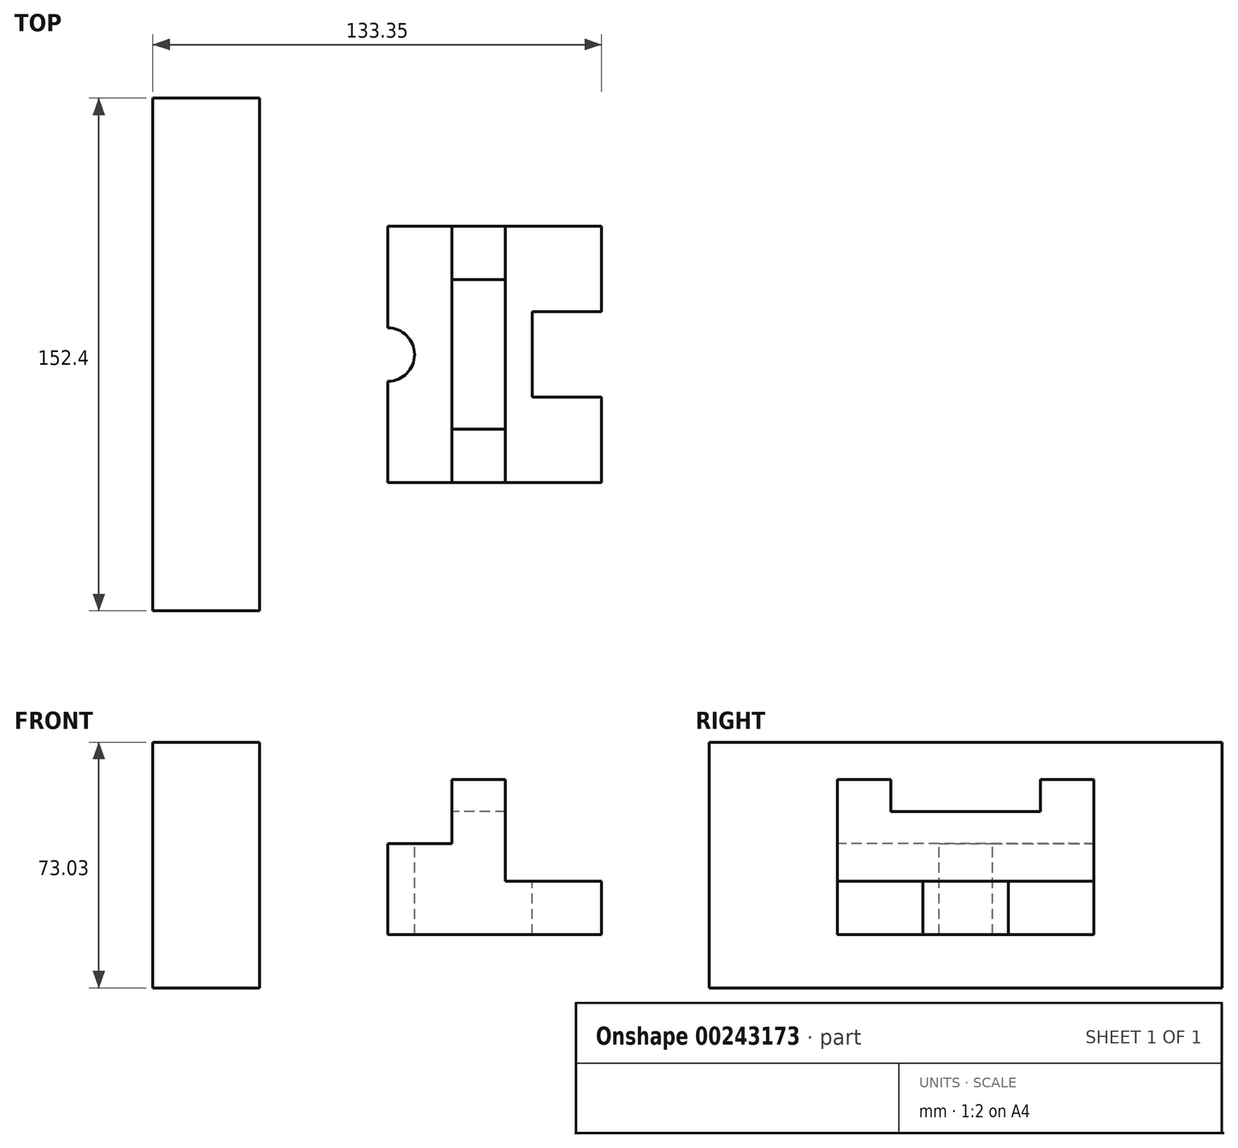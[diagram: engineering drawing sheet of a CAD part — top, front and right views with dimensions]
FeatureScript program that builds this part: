
annotation { "Feature Type Name" : "Feature", "Feature Type Description" : "" }
export const myFeature = defineFeature(function(context is Context, id is Id, definition is map)
    precondition{}
    {
        {
            var Q0;
            Q0=qCreatedBy(makeId("Top.planeOp"),FACE);
            var sketch = newSketch(context, id + "F0", { "sketchPlane" : qUnion([Q0])});
            skLineSegment(sketch, "E0", {"start": v(0, 0) * mm, "end": v(0, 76.2) * mm});
            skLineSegment(sketch, "E1", {"start": v(0, 0) * mm, "end": v(0, -76.2) * mm});
            skLineSegment(sketch, "E2", {"start": v(-127, 0) * mm, "end": v(-127, 76.2) * mm});
            skLineSegment(sketch, "E3", {"start": v(-127, 0) * mm, "end": v(-127, -76.2) * mm});
            skLineSegment(sketch, "E4", {"start": v(-127, 76.2) * mm, "end": v(0, 76.2) * mm});
            skLineSegment(sketch, "E5", {"start": v(-127, -76.2) * mm, "end": v(0, -76.2) * mm});
            skLineSegment(sketch, "E6", {"start": v(-127, 76.2) * mm, "end": v(-127, 25.4) * mm});
            skLineSegment(sketch, "E7", {"start": v(-127, -76.2) * mm, "end": v(-127, -25.4) * mm});
            skLineSegment(sketch, "E8", {"start": v(-127, -76.2) * mm, "end": v(-69.85, -76.2) * mm});
            skLineSegment(sketch, "E9", {"start": v(-127, 76.2) * mm, "end": v(-69.85, 76.2) * mm});
            skLineSegment(sketch, "E10", {"start": v(-127, 25.4) * mm, "end": v(-85.72, 25.4) * mm});
            skLineSegment(sketch, "E11", {"start": v(-127, -25.4) * mm, "end": v(-85.72, -25.4) * mm});
            skLineSegment(sketch, "E12", {"start": v(-85.72, 25.4) * mm, "end": v(-85.72, -25.4) * mm});
            skLineSegment(sketch, "E13", {"start": v(-69.85, 76.2) * mm, "end": v(-69.85, -76.2) * mm});
            skLineSegment(sketch, "E14", {"start": v(-69.85, 76.2) * mm, "end": v(-38.1, 76.2) * mm});
            skLineSegment(sketch, "E15", {"start": v(-38.1, 76.2) * mm, "end": v(-38.1, -76.2) * mm});
            skLineSegment(sketch, "E16", {"start": v(-38.1, -76.2) * mm, "end": v(-69.85, -76.2) * mm});
            skLineSegment(sketch, "E17", {"start": v(-69.85, 76.2) * mm, "end": v(-69.85, 44.45) * mm});
            skLineSegment(sketch, "E18", {"start": v(-69.85, 44.45) * mm, "end": v(-38.1, 44.45) * mm});
            skLineSegment(sketch, "E19", {"start": v(-38.1, 44.45) * mm, "end": v(-38.1, 76.2) * mm});
            skLineSegment(sketch, "E20", {"start": v(-69.85, -76.2) * mm, "end": v(-69.85, -44.45) * mm});
            skLineSegment(sketch, "E21", {"start": v(-69.85, -44.45) * mm, "end": v(-38.1, -44.45) * mm});
            skLineSegment(sketch, "E22", {"start": v(-38.1, -44.45) * mm, "end": v(-38.1, -76.2) * mm});
            skLineSegment(sketch, "E23.MirrorCS", {"start": v(127, 76.2) * mm, "end": v(127, 25.4) * mm});
            skLineSegment(sketch, "E24.MirrorCS", {"start": v(127, 25.4) * mm, "end": v(85.72, 25.4) * mm});
            skLineSegment(sketch, "E25.MirrorCS", {"start": v(127, 0) * mm, "end": v(127, 76.2) * mm});
            skLineSegment(sketch, "E26.MirrorCS", {"start": v(127, 0) * mm, "end": v(127, -76.2) * mm});
            skLineSegment(sketch, "E27.MirrorCS", {"start": v(127, -25.4) * mm, "end": v(85.72, -25.4) * mm});
            skLineSegment(sketch, "E28.MirrorCS", {"start": v(85.72, 25.4) * mm, "end": v(85.72, -25.4) * mm});
            skLineSegment(sketch, "E29.MirrorCS", {"start": v(127, 76.2) * mm, "end": v(69.85, 76.2) * mm});
            skLineSegment(sketch, "E30.MirrorCS", {"start": v(127, 76.2) * mm, "end": v(0, 76.2) * mm});
            skLineSegment(sketch, "E31.MirrorCS", {"start": v(38.1, -76.2) * mm, "end": v(69.85, -76.2) * mm});
            skLineSegment(sketch, "E32.MirrorCS", {"start": v(127, -76.2) * mm, "end": v(69.85, -76.2) * mm});
            skLineSegment(sketch, "E33.MirrorCS", {"start": v(127, -76.2) * mm, "end": v(0, -76.2) * mm});
            skLineSegment(sketch, "E34.MirrorCS", {"start": v(69.85, -44.45) * mm, "end": v(38.1, -44.45) * mm});
            skLineSegment(sketch, "E35.MirrorCS", {"start": v(69.85, 44.45) * mm, "end": v(38.1, 44.45) * mm});
            skLineSegment(sketch, "E36.MirrorCS", {"start": v(38.1, 76.2) * mm, "end": v(38.1, -76.2) * mm});
            skLineSegment(sketch, "E37.MirrorCS", {"start": v(69.85, 76.2) * mm, "end": v(69.85, -76.2) * mm});
            skCircle(sketch, "E38", {"center": v(0, 0) * mm, "radius": 15.88 * mm});
            skSolve(sketch);
        }
        {
            var Q0;
            Q0=makeQuery(id+"F0.imprint","IMPRINT",FACE,{"disambiguationData":[TD([[makeQuery(id+"F0.imprint","IMPRINT",EDGE,{"derivedFrom":sQuery(id+"F0.wireOp",EDGE,"E6")}),1.0]])]});
            var Q1;
            Q1=makeQuery(id+"F0.imprint","IMPRINT",FACE,{"disambiguationData":[TD([[makeQuery(id+"F0.imprint","IMPRINT",EDGE,{"derivedFrom":sQuery(id+"F0.wireOp",EDGE,"E2")}),-1.0]])]});
            var Q2;
            Q2=makeQuery(id+"F0.imprint","IMPRINT",FACE,{"disambiguationData":[TD([[makeQuery(id+"F0.imprint","IMPRINT",EDGE,{"derivedFrom":sQuery(id+"F0.wireOp",EDGE,"E13")}),1.0]])]});
            var Q3;
            Q3=makeQuery(id+"F0.imprint","IMPRINT",FACE,{"disambiguationData":[TD([[makeQuery(id+"F0.imprint","IMPRINT",EDGE,{"derivedFrom":sQuery(id+"F0.wireOp",EDGE,"E14")}),-1.0]])]});
            var Q4;
            Q4=makeQuery(id+"F0.imprint","IMPRINT",FACE,{"disambiguationData":[TD([[makeQuery(id+"F0.imprint","IMPRINT",EDGE,{"derivedFrom":sQuery(id+"F0.wireOp",EDGE,"E16")}),-1.0]])]});
            var Q5;
            {var subQ1=sQuery(id+"F0.wireOp",EDGE,"E4");Q5=makeQuery(id+"F0.imprint","IMPRINT",FACE,{"disambiguationData":[TD([[makeQuery(id+"F0.imprint","IMPRINT",EDGE,{"derivedFrom":subQ1}),-1.0]])]});}
            var Q6;
            {var subQ0=sQuery(id+"F0.wireOp",EDGE,"E1");var subQ1=sQuery(id+"F0.wireOp",EDGE,"E0");var subQ2=makeQuery(id+"F0.imprint","INTERSECT",VERTEX,{"derivedFrom":[subQ1,subQ0]});Q6=makeQuery(id+"F0.imprint","IMPRINT",FACE,{"disambiguationData":[TD([[makeQuery(id+"F0.imprint","IMPRINT",EDGE,{"disambiguationData":[TD([[subQ2,-1.0]])],"derivedFrom":subQ1}),1.0]])]});}
            var Q7;
            {var subQ3=sQuery(id+"F0.wireOp",EDGE,"E36.MirrorCS");var subQ12=makeQuery(id+"F0.imprint","INTERSECT",VERTEX,{"derivedFrom":[sQuery(id+"F0.wireOp",EDGE,"E35.MirrorCS"),subQ3]});Q7=makeQuery(id+"F0.imprint","IMPRINT",FACE,{"disambiguationData":[TD([[makeQuery(id+"F0.imprint","IMPRINT",EDGE,{"disambiguationData":[TD([[subQ12,1.0]])],"derivedFrom":subQ3}),-1.0]])]});}
            var Q8;
            {var subQ0=sQuery(id+"F0.wireOp",EDGE,"E1");var subQ1=sQuery(id+"F0.wireOp",EDGE,"E0");var subQ2=makeQuery(id+"F0.imprint","INTERSECT",VERTEX,{"derivedFrom":[subQ1,subQ0]});Q8=makeQuery(id+"F0.imprint","IMPRINT",FACE,{"disambiguationData":[TD([[makeQuery(id+"F0.imprint","IMPRINT",EDGE,{"disambiguationData":[TD([[subQ2,-1.0]])],"derivedFrom":subQ1}),-1.0]])]});}
            var Q9;
            {var subQ0=sQuery(id+"F0.wireOp",EDGE,"E34.MirrorCS");Q9=makeQuery(id+"F0.imprint","IMPRINT",FACE,{"disambiguationData":[TD([[makeQuery(id+"F0.imprint","IMPRINT",EDGE,{"derivedFrom":subQ0}),-1.0]])]});}
            var Q10;
            {var subQ5=sQuery(id+"F0.wireOp",EDGE,"E35.MirrorCS");Q10=makeQuery(id+"F0.imprint","IMPRINT",FACE,{"disambiguationData":[TD([[makeQuery(id+"F0.imprint","IMPRINT",EDGE,{"derivedFrom":subQ5}),-1.0]])]});}
            var Q11;
            {var subQ5=sQuery(id+"F0.wireOp",EDGE,"E34.MirrorCS");Q11=makeQuery(id+"F0.imprint","IMPRINT",FACE,{"disambiguationData":[TD([[makeQuery(id+"F0.imprint","IMPRINT",EDGE,{"derivedFrom":subQ5}),1.0]])]});}
            var Q12;
            {var subQ5=sQuery(id+"F0.wireOp",EDGE,"E24.MirrorCS");Q12=makeQuery(id+"F0.imprint","IMPRINT",FACE,{"disambiguationData":[TD([[makeQuery(id+"F0.imprint","IMPRINT",EDGE,{"derivedFrom":subQ5}),-1.0]])]});}
            var Q13;
            {var subQ4=sQuery(id+"F0.wireOp",EDGE,"E24.MirrorCS");Q13=makeQuery(id+"F0.imprint","IMPRINT",FACE,{"disambiguationData":[TD([[makeQuery(id+"F0.imprint","IMPRINT",EDGE,{"derivedFrom":subQ4}),1.0]])]});}
            extrude(context, id + "F1", {"entities" : qUnion([Q0, Q1, Q2, Q3, Q4, Q5, Q6, Q7, Q8, Q9, Q10, Q11, Q12, Q13]), "oppositeDirection" : true, "depth" : 31.75 * mm});
        }
        {
            var Q0;
            Q0=makeQuery(id+"F0.imprint","IMPRINT",FACE,{"disambiguationData":[TD([[makeQuery(id+"F0.imprint","IMPRINT",EDGE,{"derivedFrom":sQuery(id+"F0.wireOp",EDGE,"E2")}),-1.0]])]});
            var Q1;
            {var subQ4=sQuery(id+"F0.wireOp",EDGE,"E24.MirrorCS");Q1=makeQuery(id+"F0.imprint","IMPRINT",FACE,{"disambiguationData":[TD([[makeQuery(id+"F0.imprint","IMPRINT",EDGE,{"derivedFrom":subQ4}),1.0]])]});}
            extrude(context, id + "F2", {"entities" : qUnion([Q0, Q1]), "operationType" : NewBodyOperationType.REMOVE, "endBound" : BoundingType.THROUGH_ALL, "oppositeDirection" : true, "depth" : 25.4 * mm});
        }
        {
            var Q0;
            {var subQ0=sQuery(id+"F0.wireOp",EDGE,"E1");var subQ1=sQuery(id+"F0.wireOp",EDGE,"E0");var subQ2=makeQuery(id+"F0.imprint","INTERSECT",VERTEX,{"derivedFrom":[subQ1,subQ0]});Q0=makeQuery(id+"F0.imprint","IMPRINT",FACE,{"disambiguationData":[TD([[makeQuery(id+"F0.imprint","IMPRINT",EDGE,{"disambiguationData":[TD([[subQ2,-1.0]])],"derivedFrom":subQ1}),-1.0]])]});}
            var Q1;
            {var subQ0=sQuery(id+"F0.wireOp",EDGE,"E1");var subQ1=sQuery(id+"F0.wireOp",EDGE,"E0");var subQ2=makeQuery(id+"F0.imprint","INTERSECT",VERTEX,{"derivedFrom":[subQ1,subQ0]});Q1=makeQuery(id+"F0.imprint","IMPRINT",FACE,{"disambiguationData":[TD([[makeQuery(id+"F0.imprint","IMPRINT",EDGE,{"disambiguationData":[TD([[subQ2,-1.0]])],"derivedFrom":subQ1}),1.0]])]});}
            extrude(context, id + "F3", {"entities" : qUnion([Q0, Q1]), "operationType" : NewBodyOperationType.REMOVE, "endBound" : BoundingType.THROUGH_ALL, "oppositeDirection" : true, "depth" : 25.4 * mm});
        }
        {
            var Q0;
            {var subQ1=sQuery(id+"F0.wireOp",EDGE,"E4");Q0=makeQuery(id+"F0.imprint","IMPRINT",FACE,{"disambiguationData":[TD([[makeQuery(id+"F0.imprint","IMPRINT",EDGE,{"derivedFrom":subQ1}),-1.0]])]});}
            var Q1;
            {var subQ3=sQuery(id+"F0.wireOp",EDGE,"E36.MirrorCS");var subQ12=makeQuery(id+"F0.imprint","INTERSECT",VERTEX,{"derivedFrom":[sQuery(id+"F0.wireOp",EDGE,"E35.MirrorCS"),subQ3]});Q1=makeQuery(id+"F0.imprint","IMPRINT",FACE,{"disambiguationData":[TD([[makeQuery(id+"F0.imprint","IMPRINT",EDGE,{"disambiguationData":[TD([[subQ12,1.0]])],"derivedFrom":subQ3}),-1.0]])]});}
            extrude(context, id + "F4", {"entities" : qUnion([Q0, Q1]), "operationType" : NewBodyOperationType.ADD, "depth" : 22.22 * mm});
        }
        {
            var Q0;
            Q0=makeQuery(id+"F0.imprint","IMPRINT",FACE,{"disambiguationData":[TD([[makeQuery(id+"F0.imprint","IMPRINT",EDGE,{"derivedFrom":sQuery(id+"F0.wireOp",EDGE,"E14")}),-1.0]])]});
            var Q1;
            Q1=makeQuery(id+"F0.imprint","IMPRINT",FACE,{"disambiguationData":[TD([[makeQuery(id+"F0.imprint","IMPRINT",EDGE,{"derivedFrom":sQuery(id+"F0.wireOp",EDGE,"E16")}),-1.0]])]});
            var Q2;
            {var subQ5=sQuery(id+"F0.wireOp",EDGE,"E35.MirrorCS");Q2=makeQuery(id+"F0.imprint","IMPRINT",FACE,{"disambiguationData":[TD([[makeQuery(id+"F0.imprint","IMPRINT",EDGE,{"derivedFrom":subQ5}),-1.0]])]});}
            var Q3;
            {var subQ5=sQuery(id+"F0.wireOp",EDGE,"E34.MirrorCS");Q3=makeQuery(id+"F0.imprint","IMPRINT",FACE,{"disambiguationData":[TD([[makeQuery(id+"F0.imprint","IMPRINT",EDGE,{"derivedFrom":subQ5}),1.0]])]});}
            extrude(context, id + "F5", {"entities" : qUnion([Q0, Q1, Q2, Q3]), "operationType" : NewBodyOperationType.ADD, "depth" : 60.32 * mm});
        }
        {
            var Q0;
            Q0=makeQuery(id+"F0.imprint","IMPRINT",FACE,{"disambiguationData":[TD([[makeQuery(id+"F0.imprint","IMPRINT",EDGE,{"derivedFrom":sQuery(id+"F0.wireOp",EDGE,"E13")}),1.0]])]});
            var Q1;
            {var subQ0=sQuery(id+"F0.wireOp",EDGE,"E34.MirrorCS");Q1=makeQuery(id+"F0.imprint","IMPRINT",FACE,{"disambiguationData":[TD([[makeQuery(id+"F0.imprint","IMPRINT",EDGE,{"derivedFrom":subQ0}),-1.0]])]});}
            extrude(context, id + "F6", {"entities" : qUnion([Q0, Q1]), "operationType" : NewBodyOperationType.ADD, "depth" : 41.27 * mm});
        }
        {
            var Q0;
            Q0=makeQuery(id+"F1.opExtrude","SWEPT_BODY",BODY,{"disambiguationData":[OSD([sQuery(id+"F0.wireOp",EDGE,"E2"),sQuery(id+"F0.wireOp",EDGE,"E3"),sQuery(id+"F0.wireOp",EDGE,"E4"),sQuery(id+"F0.wireOp",EDGE,"E5"),sQuery(id+"F0.wireOp",EDGE,"E6"),sQuery(id+"F0.wireOp",EDGE,"E7"),sQuery(id+"F0.wireOp",EDGE,"E8"),sQuery(id+"F0.wireOp",EDGE,"E9"),sQuery(id+"F0.wireOp",EDGE,"E14"),sQuery(id+"F0.wireOp",EDGE,"E16"),sQuery(id+"F0.wireOp",EDGE,"E25.MirrorCS"),sQuery(id+"F0.wireOp",EDGE,"E26.MirrorCS"),sQuery(id+"F0.wireOp",EDGE,"E30.MirrorCS"),sQuery(id+"F0.wireOp",EDGE,"E33.MirrorCS")])]});
            var Q1;
            Q1=qCreatedBy(makeId("Origin.pointOp"),VERTEX);
            transform(context, id + "F7", {"entities" : qUnion([Q0]), "transformType" : TransformType.SCALE_UNIFORMLY, "scale" : 0.5, "scalePoint" : qUnion([Q1]), "makeCopy" : false});
        }
    });
